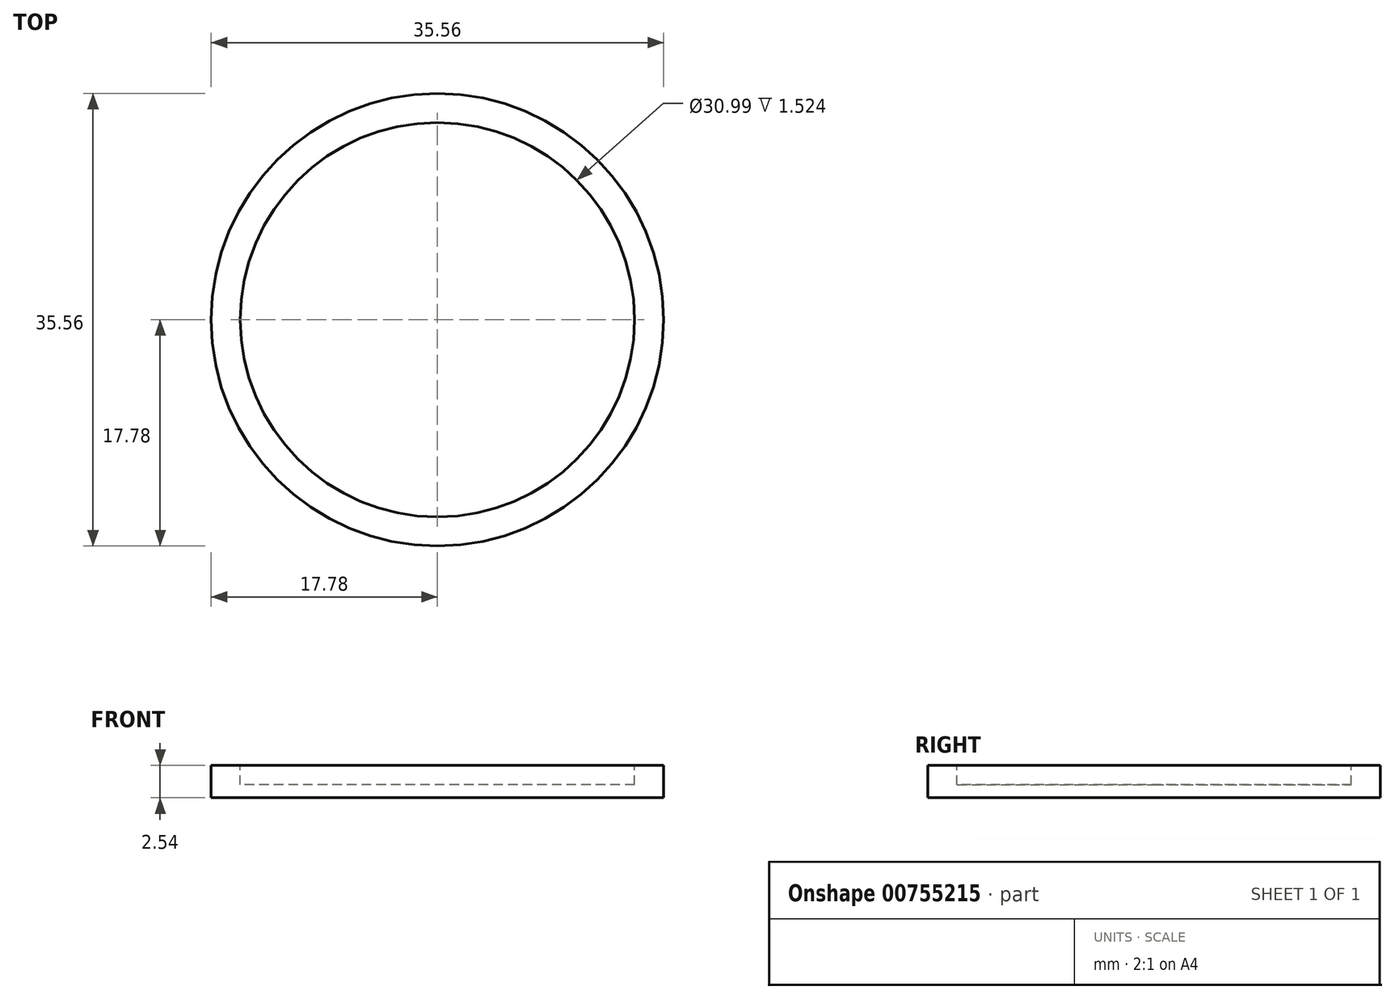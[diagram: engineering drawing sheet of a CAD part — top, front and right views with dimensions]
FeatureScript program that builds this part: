
annotation { "Feature Type Name" : "Feature", "Feature Type Description" : "" }
export const myFeature = defineFeature(function(context is Context, id is Id, definition is map)
    precondition{}
    {
        {
            var Q0;
            Q0=qCreatedBy(makeId("Top.planeOp"),FACE);
            var sketch = newSketch(context, id + "F0", { "sketchPlane" : qUnion([Q0])});
            skCircle(sketch, "E0", {"center": v(0, 0) * mm, "radius": 17.78 * mm});
            skSolve(sketch);
        }
        {
            var Q0;
            Q0=qSketchRegion(id+"F0",true);
            extrude(context, id + "F1", {"entities" : qUnion([Q0]), "flatOperationType" : FlatOperationType.REMOVE, "depth" : 2.54 * mm, "offsetDistance" : 25.4 * mm, "domain" : OperationDomain.MODEL});
        }
        {
            var Q0;
            Q0=makeQuery(id+"F1.opExtrude","CAP_FACE",FACE,{"disambiguationData":[OSD([sQuery(id+"F0.wireOp",EDGE,"E0")])],"isStart":false});
            var sketch = newSketch(context, id + "F2", { "sketchPlane" : qUnion([Q0])});
            skCircle(sketch, "E1.0", {"center": v(0, 0) * mm, "radius": 17.78 * mm, "construction": true});
            skCircle(sketch, "E2.0", {"center": v(0, 0) * mm, "radius": 15.5 * mm});
            skSolve(sketch);
        }
        {
            var Q0;
            Q0=qSketchRegion(id+"F2",true);
            extrude(context, id + "F3", {"entities" : qUnion([Q0]), "operationType" : NewBodyOperationType.REMOVE, "oppositeDirection" : true, "depth" : 1.52 * mm, "offsetDistance" : 25.4 * mm});
        }
    });
